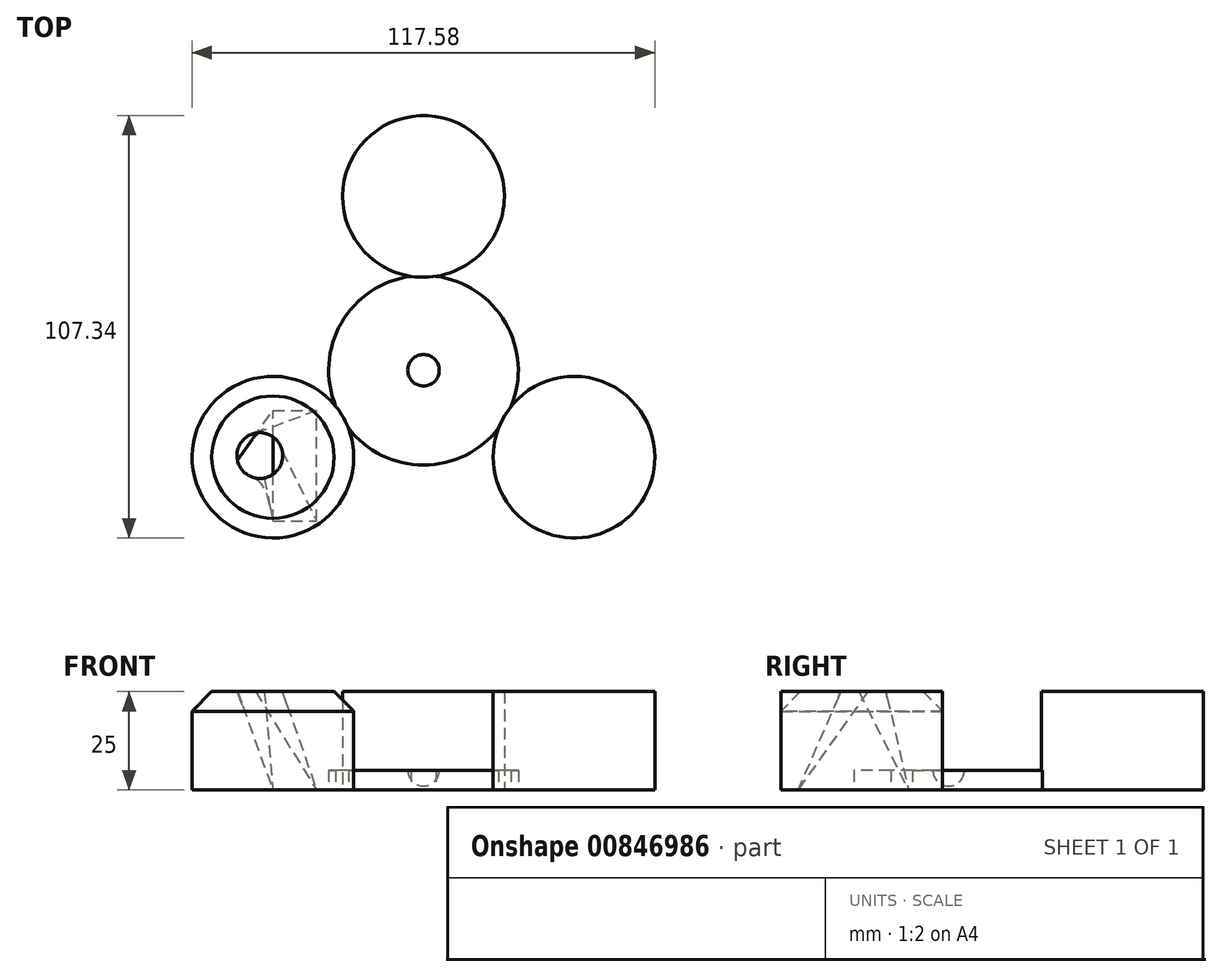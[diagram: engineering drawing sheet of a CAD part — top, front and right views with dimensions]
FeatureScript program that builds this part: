
annotation { "Feature Type Name" : "Feature", "Feature Type Description" : "" }
export const myFeature = defineFeature(function(context is Context, id is Id, definition is map)
    precondition{}
    {
        {
            var Q0;
            Q0=qCreatedBy(makeId("Top.planeOp"),FACE);
            var sketch = newSketch(context, id + "F0", { "sketchPlane" : qUnion([Q0])});
            skCircle(sketch, "E0", {"center": v(0, 0) * mm, "radius": 24.09 * mm});
            skSolve(sketch);
        }
        {
            var Q0;
            Q0=makeQuery(id+"F0.imprint","IMPRINT",FACE,{"disambiguationData":[TD([[makeQuery(id+"F0.imprint","IMPRINT",EDGE,{"derivedFrom":sQuery(id+"F0.wireOp",EDGE,"E0")}),1.0]])]});
            extrude(context, id + "F1", {"entities" : qUnion([Q0]), "depth" : 5 * mm, "offsetDistance" : 25 * mm});
        }
        {
            var Q0;
            Q0=makeQuery(id+"F1.opExtrude","CAP_FACE",FACE,{"disambiguationData":[OSD([sQuery(id+"F0.wireOp",EDGE,"E0")])],"isStart":false});
            var sketch = newSketch(context, id + "F2", { "sketchPlane" : qUnion([Q0])});
            skLineSegment(sketch, "E1", {"start": v(0, 0) * mm, "end": v(0, 10) * mm});
            skLineSegment(sketch, "E2", {"start": v(0, 10) * mm, "end": v(-10, 10) * mm});
            skLineSegment(sketch, "E3", {"start": v(-10, 10) * mm, "end": v(-10, 0) * mm});
            skLineSegment(sketch, "E4", {"start": v(-10, 0) * mm, "end": v(-10, -10) * mm});
            skLineSegment(sketch, "E5", {"start": v(-10, -10) * mm, "end": v(0, -10) * mm});
            skLineSegment(sketch, "E6", {"start": v(0, -10) * mm, "end": v(0, 0) * mm});
            skLineSegment(sketch, "E7.MirrorCS", {"start": v(10, 10) * mm, "end": v(10, 0) * mm});
            skLineSegment(sketch, "E8.MirrorCS", {"start": v(0, 10) * mm, "end": v(10, 10) * mm});
            skLineSegment(sketch, "E9.MirrorCS", {"start": v(10, 0) * mm, "end": v(10, -10) * mm});
            skLineSegment(sketch, "E10.MirrorCS", {"start": v(10, -10) * mm, "end": v(0, -10) * mm});
            skSolve(sketch);
        }
        {
            var Q0;
            Q0=makeQuery(id+"F1.opExtrude","CAP_FACE",FACE,{"disambiguationData":[OSD([sQuery(id+"F0.wireOp",EDGE,"E0")])],"isStart":false});
            var sketch = newSketch(context, id + "F3", { "sketchPlane" : qUnion([Q0])});
            skArc(sketch, "E11", {"start": v(0, -4) * mm, "mid": v(4, 0) * mm, "end": v(0, 4) * mm});
            skLineSegment(sketch, "E12", {"start": v(0, 4) * mm, "end": v(0, -4) * mm});
            skSolve(sketch);
        }
        {
            var Q0;
            Q0=makeQuery(id+"F3.imprint","IMPRINT",FACE,{"disambiguationData":[TD([[makeQuery(id+"F3.imprint","IMPRINT",EDGE,{"derivedFrom":sQuery(id+"F3.wireOp",EDGE,"E11")}),1.0]])]});
            var Q1;
            Q1=sQuery(id+"F3.wireOp",EDGE,"E12");
            revolve(context, id + "F4", {"operationType" : NewBodyOperationType.REMOVE, "surfaceOperationType" : NewSurfaceOperationType.NEW, "entities" : qUnion([Q0]), "axis" : qUnion([Q1]), "revolveType" : RevolveType.FULL, "oppositeDirection" : true});
        }
        {
            var Q0;
            Q0=qCreatedBy(makeId("Top.planeOp"),FACE);
            var sketch = newSketch(context, id + "F5", { "sketchPlane" : qUnion([Q0])});
            skCircle(sketch, "E13", {"center": v(0, 44.17) * mm, "radius": 20.54 * mm});
            skCircle(sketch, "E14.1.0", {"center": v(-38.25, -22.08) * mm, "radius": 20.54 * mm});
            skCircle(sketch, "E14.2.0", {"center": v(38.25, -22.08) * mm, "radius": 20.54 * mm});
            skPoint(sketch, "E14.center", {"position": v(0, 0) * mm});
            skSolve(sketch);
        }
        {
            var Q0;
            Q0=makeQuery(id+"F5.imprint","IMPRINT",FACE,{"disambiguationData":[TD([[makeQuery(id+"F5.imprint","IMPRINT",EDGE,{"derivedFrom":sQuery(id+"F5.wireOp",EDGE,"E14.1.0")}),1.0]])]});
            var Q1;
            Q1=makeQuery(id+"F5.imprint","IMPRINT",FACE,{"disambiguationData":[TD([[makeQuery(id+"F5.imprint","IMPRINT",EDGE,{"derivedFrom":sQuery(id+"F5.wireOp",EDGE,"E13")}),1.0]])]});
            var Q2;
            Q2=makeQuery(id+"F5.imprint","IMPRINT",FACE,{"disambiguationData":[TD([[makeQuery(id+"F5.imprint","IMPRINT",EDGE,{"derivedFrom":sQuery(id+"F5.wireOp",EDGE,"E14.2.0")}),1.0]])]});
            extrude(context, id + "F6", {"entities" : qUnion([Q0, Q1, Q2]), "operationType" : NewBodyOperationType.ADD, "depth" : 25 * mm, "offsetDistance" : 25 * mm});
        }
        {
            var Q0;
            Q0=makeQuery(id+"F6.opExtrude","CAP_EDGE",EDGE,{"disambiguationData":[OSD([sQuery(id+"F5.wireOp",EDGE,"E14.1.0")])],"isStart":false});
            chamfer(context, id + "F7", {"entities" : qUnion([Q0]), "width" : 5 * mm, "tangentPropagation" : true});
        }
        {
            var Q0;
            Q0=makeQuery(id+"F6.opExtrude","CAP_FACE",FACE,{"disambiguationData":[OSD([sQuery(id+"F5.wireOp",EDGE,"E14.1.0")])],"isStart":false});
            var sketch = newSketch(context, id + "F8", { "sketchPlane" : qUnion([Q0])});
            skCircle(sketch, "E15", {"center": v(-41.57, -21.68) * mm, "radius": 5.81 * mm});
            skSolve(sketch);
        }
        {
            var Q0;
            Q0=makeQuery(id+"F6.boolean.opBoolean","MERGE",FACE,{"derivedFrom":[makeQuery(id+"F1.opExtrude","CAP_FACE",FACE,{"disambiguationData":[OSD([sQuery(id+"F0.wireOp",EDGE,"E0")])],"isStart":true}),makeQuery(id+"F6.opExtrude","CAP_FACE",FACE,{"disambiguationData":[OSD([sQuery(id+"F5.wireOp",EDGE,"E13")])],"isStart":true}),makeQuery(id+"F6.opExtrude","CAP_FACE",FACE,{"disambiguationData":[OSD([sQuery(id+"F5.wireOp",EDGE,"E14.1.0")])],"isStart":true}),makeQuery(id+"F6.opExtrude","CAP_FACE",FACE,{"disambiguationData":[OSD([sQuery(id+"F5.wireOp",EDGE,"E14.2.0")])],"isStart":true})]});
            var sketch = newSketch(context, id + "F9", { "sketchPlane" : qUnion([Q0])});
            skLineSegment(sketch, "E16.bottom", {"start": v(-38.26, 38.31) * mm, "end": v(-27.15, 38.31) * mm});
            skLineSegment(sketch, "E16.top", {"start": v(-38.26, 10.18) * mm, "end": v(-27.15, 10.18) * mm});
            skLineSegment(sketch, "E16.left", {"start": v(-38.26, 38.31) * mm, "end": v(-38.26, 10.18) * mm});
            skLineSegment(sketch, "E16.right", {"start": v(-27.15, 38.31) * mm, "end": v(-27.15, 10.18) * mm});
            skSolve(sketch);
        }
        {
            var Q1;
            Q1=makeQuery(id+"F8.imprint","IMPRINT",FACE,{"disambiguationData":[TD([[makeQuery(id+"F8.imprint","IMPRINT",EDGE,{"derivedFrom":sQuery(id+"F8.wireOp",EDGE,"E15")}),1.0]])]});
            var Q2;
            Q2=makeQuery(id+"F9.imprint","IMPRINT",FACE,{"disambiguationData":[TD([[makeQuery(id+"F9.imprint","IMPRINT",EDGE,{"derivedFrom":sQuery(id+"F9.wireOp",EDGE,"E16.bottom")}),-1.0]])]});
            loft(context, id + "F10", {"operationType" : NewBodyOperationType.REMOVE, "sheetProfilesArray" : [{ "sheetProfileEntities" : qUnion([Q1]) }, { "sheetProfileEntities" : qUnion([Q2]) }]});
        }
    });
